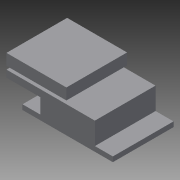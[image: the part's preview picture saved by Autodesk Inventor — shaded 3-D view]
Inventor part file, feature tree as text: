
AUTODESK INVENTOR PART (.ipt)
format: ipt  version: 2015 SP1 (Build 190203100, 203)  size: 89,088 bytes
history: native  units: in
note: dims shown in document units (in); Inventor stores cm internally (conversion verified against a paired STEP export)
features: extrude x1, sketch x1
ambient origin geometry x8: Origin, YZ Plane, XZ Plane, XY Plane, X Axis, Y Axis, Z Axis, Center Point
bodies: Solid1 (feature_tree)
feature tree (2):
  extrude  "Extrusion1"  Depth=0.7087in
  sketch  "Sketch1"  dims[d0=1.4291in d1=0.7087in d2=1.5748in d3=0.2953in d4=2.3228in d5=2.7953in d6=1.5945in d7=0.0in]
